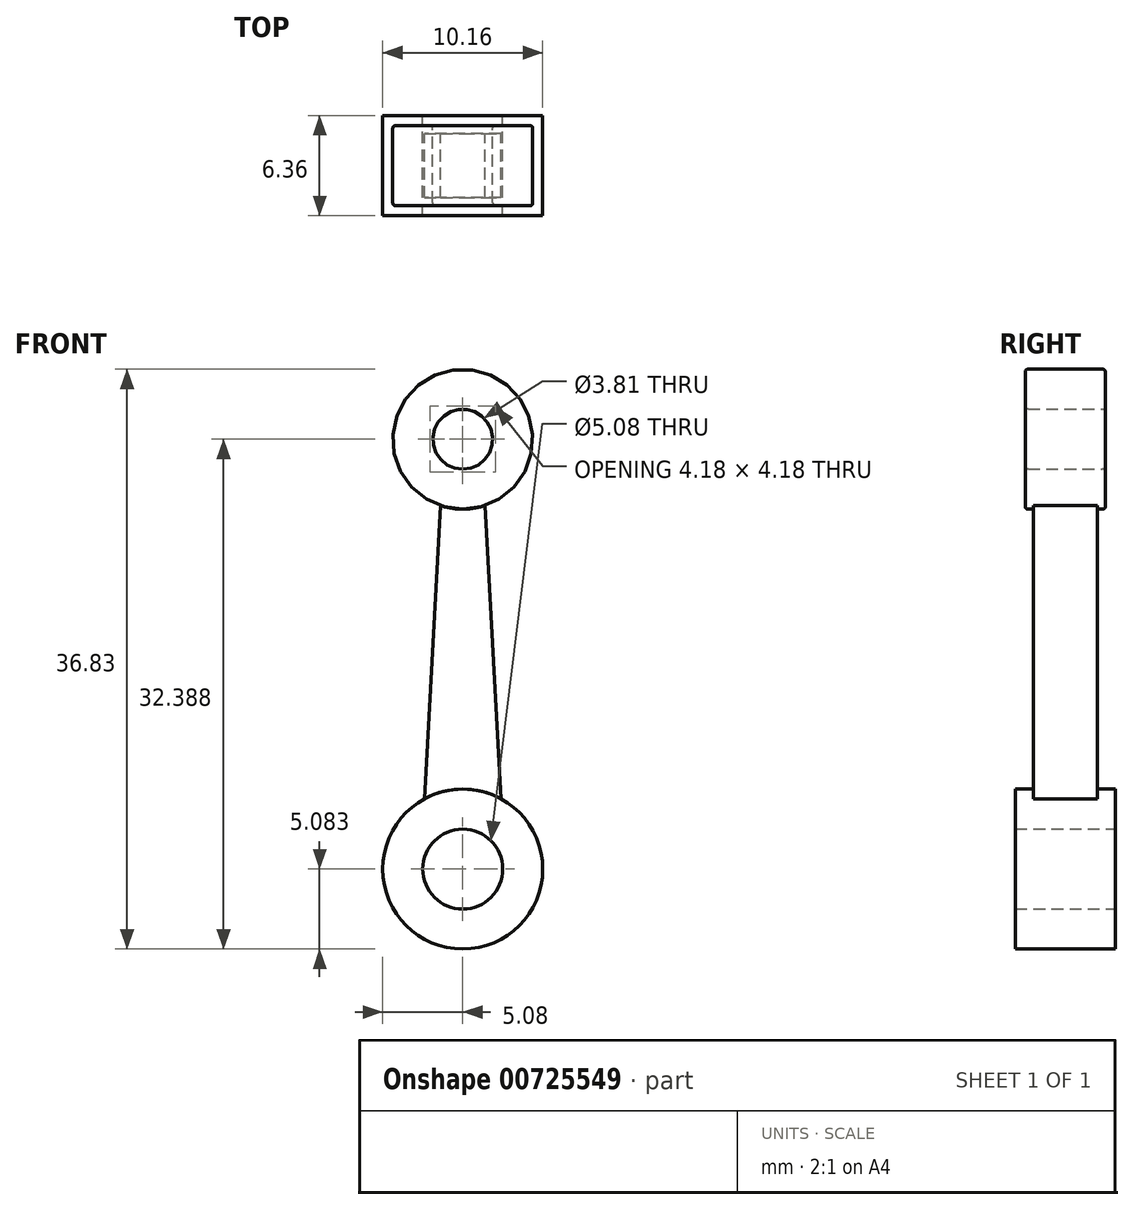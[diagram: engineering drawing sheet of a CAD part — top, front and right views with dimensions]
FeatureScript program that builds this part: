
annotation { "Feature Type Name" : "Feature", "Feature Type Description" : "" }
export const myFeature = defineFeature(function(context is Context, id is Id, definition is map)
    precondition{}
    {
        {
            var Q0;
            Q0=qCreatedBy(makeId("Front.planeOp"),FACE);
            var sketch = newSketch(context, id + "F0", { "sketchPlane" : qUnion([Q0])});
            skCircle(sketch, "E0", {"center": v(0, 5.06) * mm, "radius": 1.9 * mm});
            skCircle(sketch, "E1", {"center": v(0, 5.06) * mm, "radius": 4.45 * mm});
            skSolve(sketch);
        }
        {
            var Q0;
            Q0=makeQuery(id+"F0.imprint","IMPRINT",FACE,{"disambiguationData":[TD([[makeQuery(id+"F0.imprint","IMPRINT",EDGE,{"derivedFrom":sQuery(id+"F0.wireOp",EDGE,"E0")}),-1.0]])]});
            extrude(context, id + "F1", {"entities" : qUnion([Q0]), "endBound" : BoundingType.SYMMETRIC, "depth" : 5.08 * mm, "offsetDistance" : 25.4 * mm});
        }
        {
            var Q0;
            Q0=makeQuery(id+"F1.opExtrude","CAP_EDGE",EDGE,{"disambiguationData":[OSD([sQuery(id+"F0.wireOp",EDGE,"E0")])],"isStart":false});
            var Q1;
            Q1=makeQuery(id+"F1.opExtrude","CAP_EDGE",EDGE,{"disambiguationData":[OSD([sQuery(id+"F0.wireOp",EDGE,"E0")])],"isStart":true});
            var Q2;
            Q2=makeQuery(id+"F1.opExtrude","CAP_EDGE",EDGE,{"disambiguationData":[OSD([sQuery(id+"F0.wireOp",EDGE,"E1")])],"isStart":true});
            var Q3;
            Q3=makeQuery(id+"F1.opExtrude","CAP_EDGE",EDGE,{"disambiguationData":[OSD([sQuery(id+"F0.wireOp",EDGE,"E1")])],"isStart":false});
            fillet(context, id + "F2", {"entities" : qUnion([Q0, Q1, Q2, Q3]), "radius" : 0.18 * mm, "rho" : 0.5, "crossSection" : FilletCrossSection.CONIC, "allowEdgeOverflow" : false});
        }
        {
            var Q0;
            Q0=qCreatedBy(makeId("Front.planeOp"),FACE);
            var sketch = newSketch(context, id + "F3", { "sketchPlane" : qUnion([Q0])});
            skLineSegment(sketch, "E2", {"start": v(1.27, 3.15) * mm, "end": v(2.54, -19.7) * mm});
            skLineSegment(sketch, "E3", {"start": v(2.54, -19.7) * mm, "end": v(-2.54, -19.7) * mm});
            skLineSegment(sketch, "E4", {"start": v(-2.54, -19.7) * mm, "end": v(-1.27, 3.15) * mm});
            skLineSegment(sketch, "E5", {"start": v(-1.27, 3.15) * mm, "end": v(1.27, 3.15) * mm});
            skSolve(sketch);
        }
        {
            var Q0;
            Q0=makeQuery(id+"F3.imprint","IMPRINT",FACE,{"disambiguationData":[TD([[makeQuery(id+"F3.imprint","IMPRINT",EDGE,{"derivedFrom":sQuery(id+"F3.wireOp",EDGE,"E2")}),-1.0]])]});
            extrude(context, id + "F4", {"entities" : qUnion([Q0]), "operationType" : NewBodyOperationType.ADD, "endBound" : BoundingType.SYMMETRIC, "depth" : 4.06 * mm, "offsetDistance" : 25.4 * mm});
        }
        {
            var Q0;
            Q0=qCreatedBy(makeId("Front.planeOp"),FACE);
            var sketch = newSketch(context, id + "F5", { "sketchPlane" : qUnion([Q0])});
            skCircle(sketch, "E6", {"center": v(0, -22.25) * mm, "radius": 2.54 * mm});
            skCircle(sketch, "E7", {"center": v(0, -22.25) * mm, "radius": 5.08 * mm});
            skSolve(sketch);
        }
        {
            var Q0;
            Q0=makeQuery(id+"F5.imprint","IMPRINT",FACE,{"disambiguationData":[TD([[makeQuery(id+"F5.imprint","IMPRINT",EDGE,{"derivedFrom":sQuery(id+"F5.wireOp",EDGE,"E6")}),-1.0]])]});
            extrude(context, id + "F6", {"entities" : qUnion([Q0]), "operationType" : NewBodyOperationType.ADD, "endBound" : BoundingType.SYMMETRIC, "depth" : 6.35 * mm, "offsetDistance" : 25.4 * mm});
        }
    });
